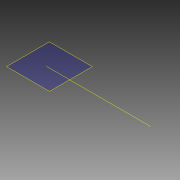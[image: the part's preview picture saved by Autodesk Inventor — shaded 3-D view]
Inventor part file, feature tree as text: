
AUTODESK INVENTOR PART (.ipt)
format: ipt  version: 2012 SP2 (Build 160219200, 219)  size: 53,760 bytes
history: native  units: in
note: dims shown in document units (in); Inventor stores cm internally (conversion verified against a paired STEP export)
features: plane x2, other x1
ambient origin geometry x8: Origin, YZ Plane, XZ Plane, XY Plane, X Axis, Y Axis, Z Axis, Center Point
feature tree (3):
  plane  "Work Plane2"
  other  "Work Axis1"
  plane  "Work Plane1"
